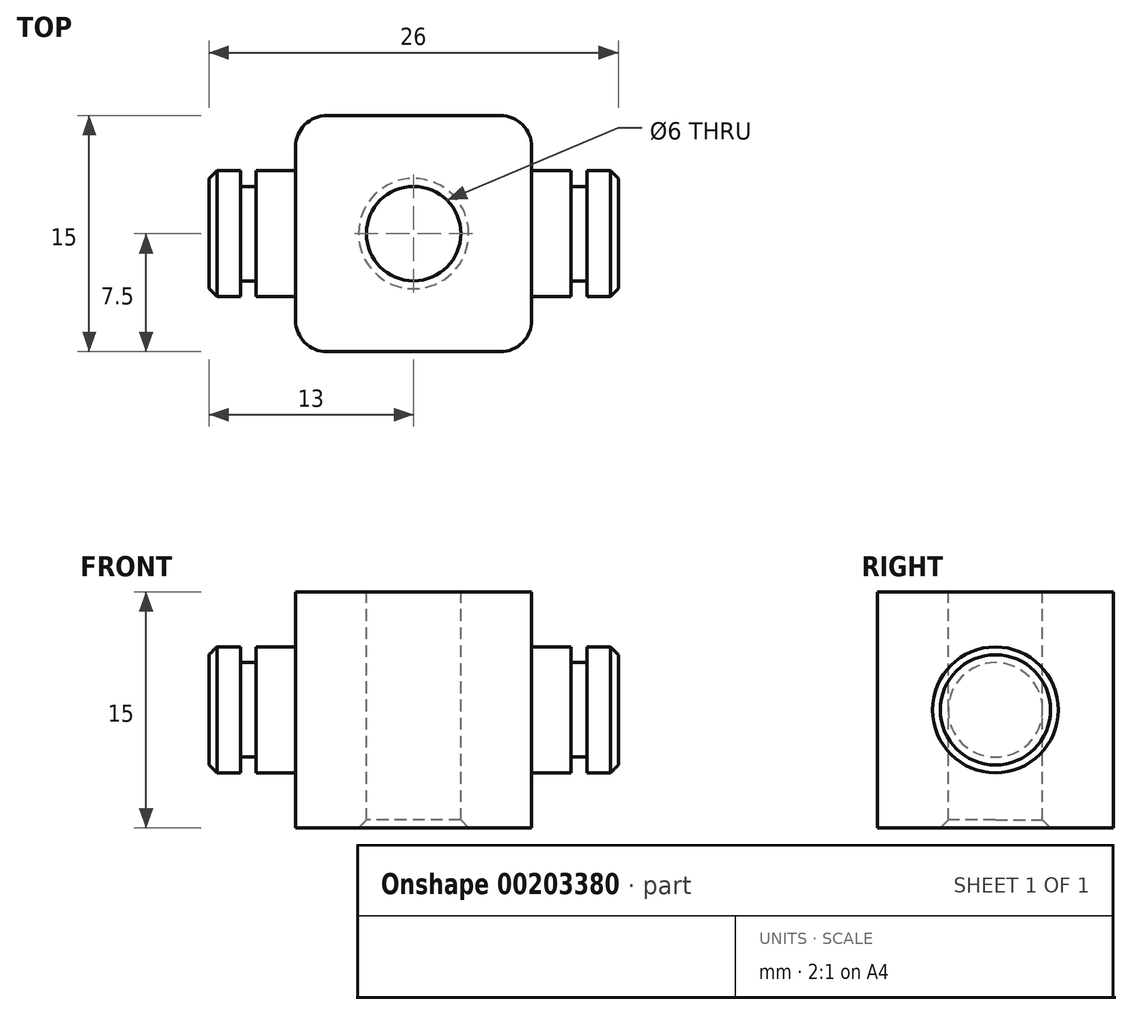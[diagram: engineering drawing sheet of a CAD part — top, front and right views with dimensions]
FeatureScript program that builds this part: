
annotation { "Feature Type Name" : "Feature", "Feature Type Description" : "" }
export const myFeature = defineFeature(function(context is Context, id is Id, definition is map)
    precondition{}
    {
        {
            var Q0;
            Q0=qCreatedBy(makeId("Front.planeOp"),FACE);
            var sketch = newSketch(context, id + "F0", { "sketchPlane" : qUnion([Q0])});
            skLineSegment(sketch, "E0.bottom", {"start": v(7.5, 7.5) * mm, "end": v(-7.5, 7.5) * mm});
            skLineSegment(sketch, "E0.top", {"start": v(7.5, -7.5) * mm, "end": v(-7.5, -7.5) * mm});
            skLineSegment(sketch, "E0.left", {"start": v(7.5, 7.5) * mm, "end": v(7.5, -7.5) * mm});
            skLineSegment(sketch, "E0.right", {"start": v(-7.5, 7.5) * mm, "end": v(-7.5, -7.5) * mm});
            skPoint(sketch, "E0.middle", {"position": v(0, 0) * mm});
            skSolve(sketch);
        }
        {
            var Q0;
            Q0=makeQuery(id+"F0.imprint","IMPRINT",FACE,{"disambiguationData":[TD([[makeQuery(id+"F0.imprint","IMPRINT",EDGE,{"derivedFrom":sQuery(id+"F0.wireOp",EDGE,"E0.bottom")}),1.0]])]});
            extrude(context, id + "F1", {"entities" : qUnion([Q0]), "endBound" : BoundingType.SYMMETRIC, "depth" : 15 * mm});
        }
        {
            var Q0;
            Q0=makeQuery(id+"F1.opExtrude","SWEPT_FACE",FACE,{"disambiguationData":[OSD([sQuery(id+"F0.wireOp",EDGE,"E0.left")])]});
            var sketch = newSketch(context, id + "F2", { "sketchPlane" : qUnion([Q0])});
            skCircle(sketch, "E1", {"center": v(0, 0) * mm, "radius": 4 * mm});
            skSolve(sketch);
        }
        {
            var Q0;
            Q0=makeQuery(id+"F2.imprint","IMPRINT",FACE,{"disambiguationData":[TD([[makeQuery(id+"F2.imprint","IMPRINT",EDGE,{"derivedFrom":sQuery(id+"F2.wireOp",EDGE,"E1")}),1.0]])]});
            extrude(context, id + "F3", {"entities" : qUnion([Q0]), "operationType" : NewBodyOperationType.ADD, "depth" : 5.5 * mm});
        }
        {
            var Q0;
            Q0=makeQuery(id+"F1.opExtrude","SWEPT_FACE",FACE,{"disambiguationData":[OSD([sQuery(id+"F0.wireOp",EDGE,"E0.right")])]});
            var sketch = newSketch(context, id + "F4", { "sketchPlane" : qUnion([Q0])});
            skCircle(sketch, "E2", {"center": v(0, 0) * mm, "radius": 4 * mm});
            skSolve(sketch);
        }
        {
            var Q0;
            Q0=makeQuery(id+"F4.imprint","IMPRINT",FACE,{"disambiguationData":[TD([[makeQuery(id+"F4.imprint","IMPRINT",EDGE,{"derivedFrom":sQuery(id+"F4.wireOp",EDGE,"E2")}),1.0]])]});
            extrude(context, id + "F5", {"entities" : qUnion([Q0]), "operationType" : NewBodyOperationType.ADD, "depth" : 5.5 * mm});
        }
        {
            var Q0;
            Q0=makeQuery(id+"F1.opExtrude","SWEPT_FACE",FACE,{"disambiguationData":[OSD([sQuery(id+"F0.wireOp",EDGE,"E0.bottom")])]});
            var sketch = newSketch(context, id + "F6", { "sketchPlane" : qUnion([Q0])});
            skCircle(sketch, "E3", {"center": v(0, 0) * mm, "radius": 3 * mm});
            skSolve(sketch);
        }
        {
            var Q0;
            Q0=makeQuery(id+"F6.imprint","IMPRINT",FACE,{"disambiguationData":[TD([[makeQuery(id+"F6.imprint","IMPRINT",EDGE,{"derivedFrom":sQuery(id+"F6.wireOp",EDGE,"E3")}),1.0]])]});
            extrude(context, id + "F7", {"entities" : qUnion([Q0]), "operationType" : NewBodyOperationType.REMOVE, "endBound" : BoundingType.THROUGH_ALL, "oppositeDirection" : true, "depth" : 25 * mm});
        }
        {
            var Q0;
            Q0=qCreatedBy(makeId("Front.planeOp"),FACE);
            var sketch = newSketch(context, id + "F8", { "sketchPlane" : qUnion([Q0])});
            skLineSegment(sketch, "E4", {"start": v(10, 4) * mm, "end": v(10, 3) * mm});
            skLineSegment(sketch, "E5", {"start": v(11, 3) * mm, "end": v(11, 4) * mm});
            skLineSegment(sketch, "E6", {"start": v(11, 4) * mm, "end": v(10, 4) * mm});
            skLineSegment(sketch, "E7", {"start": v(10, 3) * mm, "end": v(11, 3) * mm});
            skLineSegment(sketch, "E8.0", {"start": v(13, 4) * mm, "end": v(13, -4) * mm});
            skLineSegment(sketch, "E9", {"start": v(7.5, 4) * mm, "end": v(13, 4) * mm});
            skSolve(sketch);
        }
        {
            var Q0;
            {var subQ0=sQuery(id+"F8.wireOp",EDGE,"E4");Q0=makeQuery(id+"F8.imprint","IMPRINT",FACE,{"disambiguationData":[TD([[makeQuery(id+"F8.imprint","IMPRINT",EDGE,{"derivedFrom":subQ0}),1.0]])]});}
            var Q1;
            Q1=makeQuery(id+"F3.opExtrude","CAP_EDGE",EDGE,{"disambiguationData":[OSD([sQuery(id+"F2.wireOp",EDGE,"E1")])],"isStart":false});
            revolve(context, id + "F9", {"operationType" : NewBodyOperationType.REMOVE, "entities" : qUnion([Q0]), "axis" : qUnion([Q1]), "revolveType" : RevolveType.FULL, "oppositeDirection" : true});
        }
        {
            var Q0;
            Q0=qCreatedBy(makeId("Front.planeOp"),FACE);
            var sketch = newSketch(context, id + "F10", { "sketchPlane" : qUnion([Q0])});
            skLineSegment(sketch, "E10.bottom", {"start": v(-10, 3) * mm, "end": v(-11, 3) * mm});
            skLineSegment(sketch, "E10.top", {"start": v(-10, 4) * mm, "end": v(-11, 4) * mm});
            skLineSegment(sketch, "E10.left", {"start": v(-10, 3) * mm, "end": v(-10, 4) * mm});
            skLineSegment(sketch, "E10.right", {"start": v(-11, 3) * mm, "end": v(-11, 4) * mm});
            skPoint(sketch, "E10.middle", {"position": v(-10.5, 3.5) * mm});
            skLineSegment(sketch, "E11", {"start": v(-13, 4) * mm, "end": v(-7.5, 4) * mm});
            skSolve(sketch);
        }
        {
            var Q0;
            Q0=makeQuery(id+"F10.imprint","IMPRINT",FACE,{"disambiguationData":[TD([[makeQuery(id+"F10.imprint","IMPRINT",EDGE,{"derivedFrom":sQuery(id+"F10.wireOp",EDGE,"E10.bottom")}),-1.0]])]});
            var Q1;
            Q1=makeQuery(id+"F5.opExtrude","CAP_EDGE",EDGE,{"disambiguationData":[OSD([sQuery(id+"F4.wireOp",EDGE,"E2")])],"isStart":false});
            revolve(context, id + "F11", {"operationType" : NewBodyOperationType.REMOVE, "entities" : qUnion([Q0]), "axis" : qUnion([Q1]), "revolveType" : RevolveType.FULL, "oppositeDirection" : true});
        }
        {
            var Q0;
            Q0=makeQuery(id+"F3.opExtrude","CAP_EDGE",EDGE,{"disambiguationData":[OSD([sQuery(id+"F2.wireOp",EDGE,"E1")])],"isStart":false});
            var Q1;
            Q1=makeQuery(id+"F5.opExtrude","CAP_EDGE",EDGE,{"disambiguationData":[OSD([sQuery(id+"F4.wireOp",EDGE,"E2")])],"isStart":false});
            chamfer(context, id + "F12", {"entities" : qUnion([Q0, Q1]), "width" : 0.5 * mm, "tangentPropagation" : true});
        }
        {
            var Q0;
            Q0=makeQuery(id+"F1.opExtrude","CAP_EDGE",EDGE,{"disambiguationData":[OSD([sQuery(id+"F0.wireOp",EDGE,"E0.right")])],"isStart":false});
            var Q1;
            Q1=makeQuery(id+"F1.opExtrude","CAP_EDGE",EDGE,{"disambiguationData":[OSD([sQuery(id+"F0.wireOp",EDGE,"E0.right")])],"isStart":true});
            var Q2;
            Q2=makeQuery(id+"F1.opExtrude","CAP_EDGE",EDGE,{"disambiguationData":[OSD([sQuery(id+"F0.wireOp",EDGE,"E0.left")])],"isStart":true});
            var Q3;
            Q3=makeQuery(id+"F1.opExtrude","CAP_EDGE",EDGE,{"disambiguationData":[OSD([sQuery(id+"F0.wireOp",EDGE,"E0.left")])],"isStart":false});
            fillet(context, id + "F13", {"entities" : qUnion([Q0, Q1, Q2, Q3]), "radius" : 2 * mm, "tangentPropagation" : true, "allowEdgeOverflow" : false});
        }
        {
            var Q0;
            Q0=makeQuery(id+"F7.boolean.opBoolean","COPY",EDGE,{"derivedFrom":makeQuery(id+"F7.opExtrude","CAP_EDGE",EDGE,{"disambiguationData":[OSD([sQuery(id+"F6.wireOp",EDGE,"E3")])],"isStart":true})});
            var Q1;
            Q1=makeQuery(id+"F7.boolean.opBoolean","INTERSECT",EDGE,{"derivedFrom":[makeQuery(id+"F1.opExtrude","SWEPT_FACE",FACE,{"disambiguationData":[OSD([sQuery(id+"F0.wireOp",EDGE,"E0.top")])]}),makeQuery(id+"F7.opExtrude","SWEPT_FACE",FACE,{"disambiguationData":[OSD([sQuery(id+"F6.wireOp",EDGE,"E3")])]})]});
            chamfer(context, id + "F14", {"entities" : qUnion([Q0, Q1]), "width" : 0.5 * mm, "tangentPropagation" : true});
        }
    });
